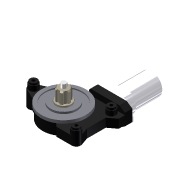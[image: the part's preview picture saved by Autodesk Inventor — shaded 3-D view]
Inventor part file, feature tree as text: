
AUTODESK INVENTOR PART (.ipt)
format: ipt  version: 2011 SP1 (Build 150282100, 282)  size: 438,784 bytes
history: native  units: mm
features: extrude x20, sketch x14, plane x4, chamfer x3, projected_geometry x3, pattern_circular x2, revolve x1, hole x1, other x1, fillet x1
ambient origin geometry x8: Origin, YZ Plane, XZ Plane, XY Plane, X Axis, Y Axis, Z Axis, Center Point
bodies: Solid1 (feature_tree)
feature tree (50):
  sketch  "Sketch1"  dims[d0=72.0mm d1=4.8mm d2=0.0mm]
  extrude  "Extrusion1"  Depth=4.8mm TaperAngle=0.0deg
  extrude  "Extrusion2"  Depth=42.0mm
  extrude  "Extrusion3"  Depth=1.9mm TaperAngle=0.0deg
  extrude  "Extrusion4"  Depth=23.8mm
  extrude  "Extrusion5"  Depth=16.4mm
  extrude  "Extrusion6"  Depth=8.0mm
  extrude  "Extrusion7"  Depth=19.9mm
  chamfer  "Chamfer1"  Distance=6.7mm
  pattern_circular  "Circular Pattern1"  Count=6 Angle=360.0deg
  sketch  "Sketch6"  dims[d14=18.0mm d15=0.0mm d16=8.0mm]
  extrude  "Extrusion8"  Depth=14.2mm
  plane  "Work Plane1"
  extrude  "Extrusion9"  Depth=56.76mm
  extrude  "Extrusion10"  Depth=37.0mm
  extrude  "Extrusion11"  Depth=25.0mm
  revolve  "Revolution1"  [1 undecoded]
  extrude  "Extrusion20"  Depth=30.5mm
  pattern_circular  "Circular Pattern2"  [2 undecoded]
  extrude  "Extrusion12"  Depth=15.0mm
  extrude  "Extrusion13"  Depth=18.6mm TaperAngle=0.0deg
  hole  "Hole2"  [1 undecoded]
  plane  "Work Plane4"
  extrude  "Extrusion19"  Depth=17.0mm TaperAngle=0.0deg
  other  "Work Axis1"
  extrude  "Extrusion14"  Depth=14.0mm TaperAngle=0.0deg
  chamfer  "Chamfer2"  Distance=19.5mm
  chamfer  "Chamfer3"  Distance=3.0mm
  fillet  "Fillet1"  Radius=3.0mm
  sketch  "Sketch13"  dims[d31=101.5mm d32=56.76mm]
  extrude  "Extrusion15"  Depth=11.9mm
  extrude  "Extrusion16"  Depth=3.0mm TaperAngle=0.0deg
  extrude  "Extrusion17"  [1 undecoded]
  extrude  "Extrusion18"  Depth=31.0mm
  sketch  "Sketch2"  dims[d3=60.0mm d4=42.0mm]
  sketch  "Sketch3"  dims[d5=25.8mm d6=1.9mm d7=0.0mm]
  sketch  "Sketch4"  dims[d8=1.2mm d9=0.0mm d10=23.8mm]
  sketch  "Sketch5"  dims[d11=3.0mm d12=0.0mm d13=16.4mm]
  sketch  "Sketch7"  dims[d17=6.7mm d18=0.0mm d19=19.9mm]
  sketch  "Sketch10"  dims[d20=4.0mm d21=6.7mm d22=0.0mm]
  projected_geometry  "Projected Loop4"
  sketch  "Sketch11"  dims[d23=1.75mm d24=2.0mm d25=45.0deg d26=60.0mm d27=360.0deg]
  projected_geometry  "Projected Loop5"
  projected_geometry  "Projected Loop6"
  plane  "Work Plane2"
  plane  "Work Plane3"
  sketch  "Sketch12"  dims[d29=68.0mm d30=14.2mm]
  sketch  "Sketch14"  dims[d33=16.3mm d34=37.0mm]
  sketch  "Sketch15"  dims[d35=135.0deg d36=25.0mm]
  sketch  "Sketch16"  dims[d37=10.0mm d38=63.0mm d39=30.5mm d40=13.2mm d41=15.0mm d42=18.6mm d43=0.0mm d44=6.0mm d45=17.0mm d46=0.0mm d47=14.0mm d48=0.0mm d49=19.5mm d50=3.0mm d51=0.0mm d52=3.0mm d53=0.0mm d61=11.9mm d62=3.0mm d63=0.0mm d64=5.0mm d65=6.0mm d66=4.0mm d67=2.0mm d68=90.0deg d69=8.0mm d70=20.594885mm d71=-17.0mm d73=31.0mm d74=12.0mm d75=0.0mm d76=40.0mm d78=6.0mm d79=9.0mm d80=45.0deg d81=6.0mm d82=9.0mm d83=45.0deg d84=6.5mm d85=34.9mm d86=19.95mm d88=3.75mm d89=17.45mm d90=3.0mm d91=10.0mm d92=2.0mm d93=0.0mm d94=15.0mm d95=0.0mm d96=60.0mm d97=0.0mm d98=67.0mm d99=0.0mm d100=0.2mm d101=3.55mm d102=-36.2mm d103=67.0mm d104=0.0mm d106=19.6mm d107=3.8mm d108=90.0deg d109=30.0deg d110=1.0mm d111=19.0mm d112=2.0mm d113=1.0mm d114=4.5mm d115=0.0mm d116=120.0mm d117=360.0deg]
note: 5 required parameter values undecoded (feature->parameter linkage not recoverable at this tier; creation-order binding heuristic only, values carry confidence <= 0.55)